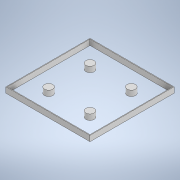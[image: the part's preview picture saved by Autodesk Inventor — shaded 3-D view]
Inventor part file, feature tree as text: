
AUTODESK INVENTOR PART (.ipt)
format: ipt  version: 2020 (Build 240168000, 168)  size: 117,760 bytes
history: native  units: mm
features: extrude x1, sketch x1
ambient origin geometry x8: Origin, YZ Plane, XZ Plane, XY Plane, X Axis, Y Axis, Z Axis, Center Point
bodies: Solid1 (feature_tree)
feature tree (2):
  extrude  "Extrusion1"  Depth=6000.0mm
  sketch  "Sketch1"  dims[d0=6000.0mm d1=6000.0mm d2=50.0mm d3=600.0mm d4=600.0mm d5=600.0mm d6=600.0mm d7=3000.0mm d8=400.0mm d9=0.0mm]
